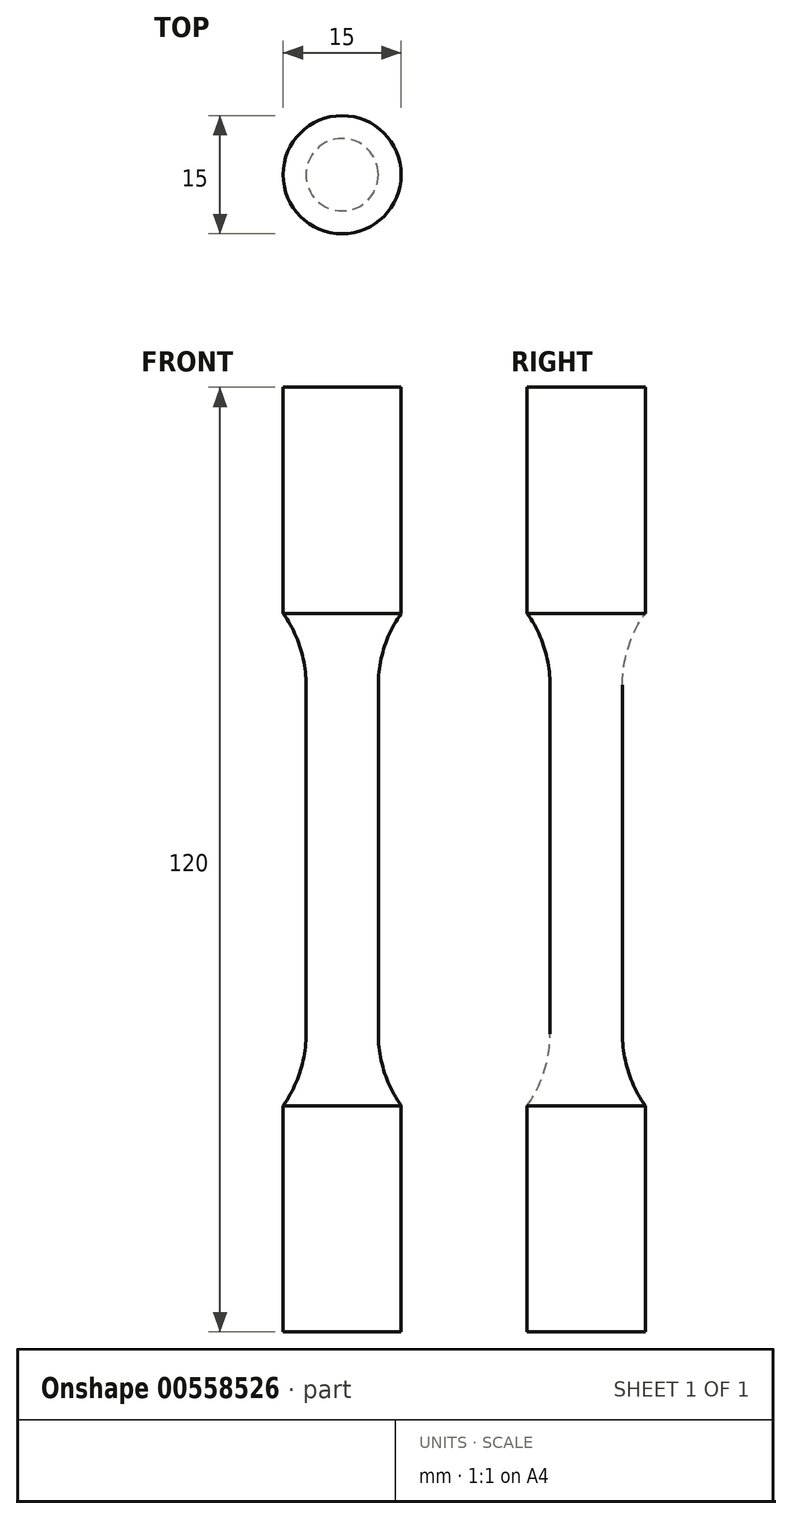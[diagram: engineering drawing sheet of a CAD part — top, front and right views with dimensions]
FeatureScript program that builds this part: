
annotation { "Feature Type Name" : "Feature", "Feature Type Description" : "" }
export const myFeature = defineFeature(function(context is Context, id is Id, definition is map)
    precondition{}
    {
        {
            var Q0;
            Q0=qCreatedBy(makeId("Front.planeOp"),FACE);
            var sketch = newSketch(context, id + "F0", { "sketchPlane" : qUnion([Q0])});
            skLineSegment(sketch, "E0.bottom", {"start": v(0, 0) * mm, "end": v(7.5, 0) * mm});
            skLineSegment(sketch, "E0.top", {"start": v(0, 120) * mm, "end": v(7.5, 120) * mm});
            skLineSegment(sketch, "E0.left", {"start": v(0, 0) * mm, "end": v(0, 120) * mm});
            skLineSegment(sketch, "E0.right", {"start": v(7.5, 0) * mm, "end": v(7.5, 120) * mm});
            skSolve(sketch);
        }
        {
            var Q0;
            Q0=makeQuery(id+"F0.imprint","IMPRINT",FACE,{"disambiguationData":[TD([[makeQuery(id+"F0.imprint","IMPRINT",EDGE,{"derivedFrom":sQuery(id+"F0.wireOp",EDGE,"E0.bottom")}),1.0]])]});
            var Q1;
            Q1=sQuery(id+"F0.wireOp",EDGE,"E0.left");
            revolve(context, id + "F1", {"entities" : qUnion([Q0]), "axis" : qUnion([Q1]), "revolveType" : RevolveType.FULL});
        }
        {
            var Q0;
            Q0=qCreatedBy(makeId("Front.planeOp"),FACE);
            var sketch = newSketch(context, id + "F2", { "sketchPlane" : qUnion([Q0])});
            skLineSegment(sketch, "E1", {"start": v(-4.6, 37.85) * mm, "end": v(-4.6, 82.15) * mm});
            skLineSegment(sketch, "E2", {"start": v(-17.63, 60) * mm, "end": v(22.15, 60) * mm, "construction": true});
            skPoint(sketch, "E3", {"position": v(-4.6, 60) * mm});
            skArc(sketch, "E4", {"start": v(-20.4, 22.04) * mm, "mid": v(-9.23, 26.67) * mm, "end": v(-4.6, 37.85) * mm});
            skArc(sketch, "E5", {"start": v(-4.6, 82.15) * mm, "mid": v(-9.23, 93.33) * mm, "end": v(-20.4, 97.96) * mm});
            skLineSegment(sketch, "E6", {"start": v(-20.4, 22.04) * mm, "end": v(-20.4, 97.96) * mm});
            skLineSegment(sketch, "E7", {"start": v(0, -15.63) * mm, "end": v(0, 129.99) * mm, "construction": true});
            skSolve(sketch);
        }
        {
            var Q0;
            Q0=makeQuery(id+"F2.imprint","IMPRINT",FACE,{"disambiguationData":[TD([[makeQuery(id+"F2.imprint","IMPRINT",EDGE,{"derivedFrom":sQuery(id+"F2.wireOp",EDGE,"E1")}),1.0]])]});
            var Q1;
            Q1=sQuery(id+"F2.wireOp",EDGE,"E7");
            revolve(context, id + "F3", {"operationType" : NewBodyOperationType.REMOVE, "entities" : qUnion([Q0]), "axis" : qUnion([Q1]), "revolveType" : RevolveType.FULL, "oppositeDirection" : true});
        }
    });
